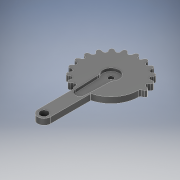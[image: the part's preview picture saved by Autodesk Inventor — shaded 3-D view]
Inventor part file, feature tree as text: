
AUTODESK INVENTOR PART (.ipt)
format: ipt  version: 2021 (Build 250183000, 183)  size: 282,112 bytes
history: native  units: mm
features: extrude x4, sketch x3, fillet x1, pattern_circular x1
ambient origin geometry x8: Origin, YZ Plane, XZ Plane, XY Plane, X Axis, Y Axis, Z Axis, Center Point
bodies: Solid1 (feature_tree)
feature tree (9):
  extrude  "Extrusion1"  Depth=20.0mm
  extrude  "Extrusion2"  Depth=2.5mm
  fillet  "Fillet1"  Radius=3.0mm
  pattern_circular  "Circular Pattern1"  [2 undecoded]
  extrude  "Extrusion6"  Depth=3.0mm TaperAngle=0.0deg
  extrude  "Extrusion7"  Depth=1.0mm
  sketch  "Sketch1"  dims[d0=27.5mm d1=20.0mm]
  sketch  "Sketch9"  dims[d2=6.5mm d3=2.5mm d4=3.0mm d5=0.0mm]
  sketch  "Sketch11"  dims[d6=2.25mm d7=1.6mm d9=3.0mm d10=0.0mm d11=1.0mm d12=150.0mm d13=43.633231mm d15=1.501956mm d16=4.0mm d41=5.0mm d42=1.2mm d43=0.0mm d44=2.0mm d46=3.6mm d47=5.0mm d48=15.6mm d49=0.5mm d50=1.5mm d51=0.0mm]
note: 2 required parameter values undecoded (feature->parameter linkage not recoverable at this tier; creation-order binding heuristic only, values carry confidence <= 0.55)
